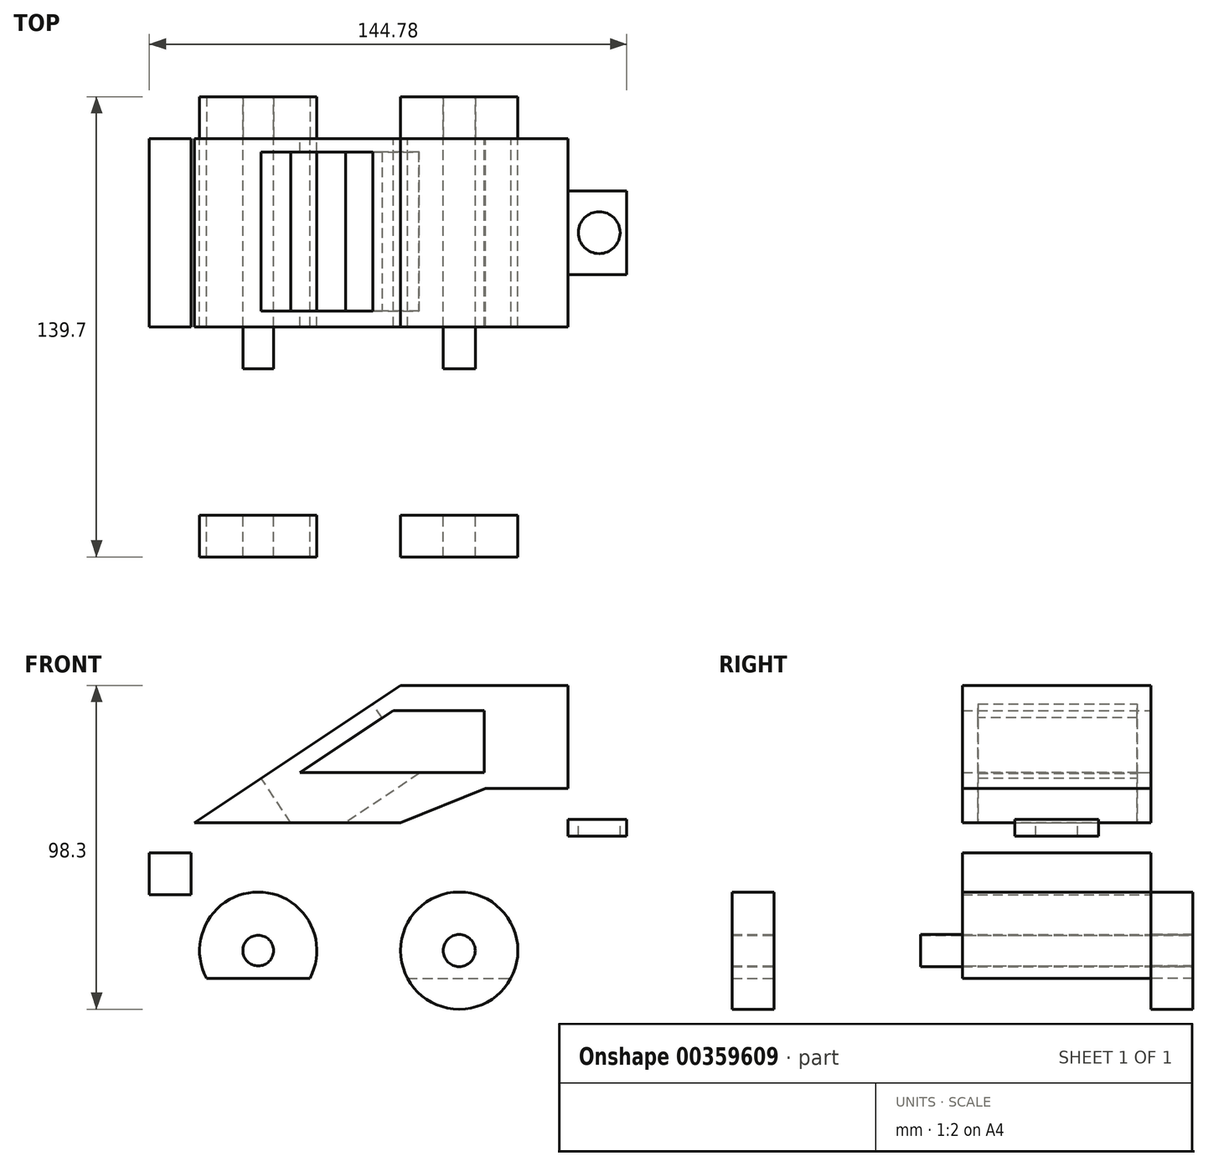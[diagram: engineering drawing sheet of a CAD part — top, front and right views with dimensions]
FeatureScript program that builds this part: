
annotation { "Feature Type Name" : "Feature", "Feature Type Description" : "" }
export const myFeature = defineFeature(function(context is Context, id is Id, definition is map)
    precondition{}
    {
        {
            var Q0;
            Q0=qCreatedBy(makeId("Front.planeOp"),FACE);
            var sketch = newSketch(context, id + "F0", { "sketchPlane" : qUnion([Q0])});
            skLineSegment(sketch, "E0.bottom", {"start": v(13.82, 40.44) * mm, "end": v(64.62, 40.44) * mm});
            skLineSegment(sketch, "E0.top", {"start": v(-62.38, -48.46) * mm, "end": v(64.62, -48.46) * mm});
            skLineSegment(sketch, "E0.left", {"start": v(-62.38, -10.36) * mm, "end": v(-62.38, -48.46) * mm});
            skLineSegment(sketch, "E0.right", {"start": v(64.62, 40.44) * mm, "end": v(64.62, -48.46) * mm});
            skLineSegment(sketch, "E1", {"start": v(-62.38, -10.36) * mm, "end": v(13.82, 40.44) * mm});
            skLineSegment(sketch, "E2.bottom", {"start": v(-62.38, -10.36) * mm, "end": v(-49.68, -10.36) * mm});
            skLineSegment(sketch, "E2.top", {"start": v(-62.38, -23.06) * mm, "end": v(-49.68, -23.06) * mm});
            skLineSegment(sketch, "E2.left", {"start": v(-62.38, -10.36) * mm, "end": v(-62.38, -23.06) * mm});
            skLineSegment(sketch, "E2.right", {"start": v(-49.68, -10.36) * mm, "end": v(-49.68, -23.06) * mm});
            skLineSegment(sketch, "E3", {"start": v(-62.38, -10.36) * mm, "end": v(13.82, -10.36) * mm});
            skLineSegment(sketch, "E4", {"start": v(13.82, -1.24) * mm, "end": v(-48.7, -1.24) * mm});
            skLineSegment(sketch, "E5", {"start": v(39.22, 14) * mm, "end": v(39.22, 32.82) * mm});
            skLineSegment(sketch, "E6", {"start": v(39.22, 14) * mm, "end": v(-16.66, 14) * mm});
            skLineSegment(sketch, "E7", {"start": v(39.22, 32.82) * mm, "end": v(11.58, 32.82) * mm});
            skLineSegment(sketch, "E8", {"start": v(11.58, 32.82) * mm, "end": v(-16.66, 14) * mm});
            skCircle(sketch, "E9", {"center": v(-29.36, -40.08) * mm, "radius": 17.78 * mm});
            skCircle(sketch, "E10", {"center": v(31.6, -40.08) * mm, "radius": 17.78 * mm});
            skCircle(sketch, "E11", {"center": v(-29.36, -40.08) * mm, "radius": 4.65 * mm});
            skCircle(sketch, "E12", {"center": v(31.6, -40.08) * mm, "radius": 4.86 * mm});
            skPoint(sketch, "E13.orphan", {"position": v(-62.38, 40.44) * mm});
            skLineSegment(sketch, "E14", {"start": v(13.82, -1.24) * mm, "end": v(39.6, 9.12) * mm});
            skLineSegment(sketch, "E15", {"start": v(39.6, 9.12) * mm, "end": v(64.62, 9.12) * mm});
            skLineSegment(sketch, "E16", {"start": v(64.62, 0) * mm, "end": v(39.6, 0) * mm});
            skLineSegment(sketch, "E17", {"start": v(39.6, 0) * mm, "end": v(13.82, -10.36) * mm});
            skSolve(sketch);
        }
        {
            var Q0;
            {var subQ1=sQuery(id+"F0.wireOp",EDGE,"E0.bottom");Q0=makeQuery(id+"F0.imprint","IMPRINT",FACE,{"disambiguationData":[TD([[makeQuery(id+"F0.imprint","IMPRINT",EDGE,{"derivedFrom":subQ1}),-1.0]])]});}
            var Q1;
            {var subQ5=sQuery(id+"F0.wireOp",EDGE,"E0.left");Q1=makeQuery(id+"F0.imprint","IMPRINT",FACE,{"disambiguationData":[TD([[makeQuery(id+"F0.imprint","IMPRINT",EDGE,{"derivedFrom":subQ5}),1.0]])]});}
            var Q2;
            Q2=makeQuery(id+"F0.imprint","IMPRINT",FACE,{"disambiguationData":[TD([[makeQuery(id+"F0.imprint","IMPRINT",EDGE,{"derivedFrom":sQuery(id+"F0.wireOp",EDGE,"E11")}),-1.0]])]});
            var Q3;
            Q3=makeQuery(id+"F0.imprint","IMPRINT",FACE,{"disambiguationData":[TD([[makeQuery(id+"F0.imprint","IMPRINT",EDGE,{"derivedFrom":sQuery(id+"F0.wireOp",EDGE,"E12")}),-1.0]])]});
            extrude(context, id + "F1", {"entities" : qUnion([Q0, Q1, Q2, Q3]), "depth" : 57.15 * mm});
        }
        {
            var Q0;
            Q0=makeQuery(id+"F0.imprint","IMPRINT",FACE,{"disambiguationData":[TD([[makeQuery(id+"F0.imprint","IMPRINT",EDGE,{"derivedFrom":sQuery(id+"F0.wireOp",EDGE,"E2.top")}),1.0]])]});
            var Q1;
            {var subQ4=sQuery(id+"F0.wireOp",EDGE,"4A5fvVYB-3RyO-qsuN-9SgG-2Ac1qKv1juyk");Q1=makeQuery(id+"F0.imprint","IMPRINT",FACE,{"disambiguationData":[TD([[makeQuery(id+"F0.imprint","IMPRINT",EDGE,{"derivedFrom":subQ4}),-1.0]])]});}
            extrude(context, id + "F2", {"entities" : qUnion([Q0, Q1]), "depth" : 57.15 * mm});
        }
        {
            var Q0;
            Q0=makeQuery(id+"F0.imprint","IMPRINT",FACE,{"disambiguationData":[TD([[makeQuery(id+"F0.imprint","IMPRINT",EDGE,{"derivedFrom":sQuery(id+"F0.wireOp",EDGE,"E2.top")}),1.0]])]});
            extrude(context, id + "F3", {"entities" : qUnion([Q0]), "depth" : 57.15 * mm});
        }
        {
            var Q0;
            Q0=makeQuery(id+"F0.imprint","IMPRINT",FACE,{"disambiguationData":[TD([[makeQuery(id+"F0.imprint","IMPRINT",EDGE,{"derivedFrom":sQuery(id+"F0.wireOp",EDGE,"E11")}),-1.0]])]});
            var Q1;
            Q1=makeQuery(id+"F0.imprint","IMPRINT",FACE,{"disambiguationData":[TD([[makeQuery(id+"F0.imprint","IMPRINT",EDGE,{"derivedFrom":sQuery(id+"F0.wireOp",EDGE,"E12")}),-1.0]])]});
            var Q2;
            {var subQ0=sQuery(id+"F0.wireOp",EDGE,"E10");var subQ1=sQuery(id+"F0.wireOp",EDGE,"E0.top");var subQ2=makeQuery(id+"F0.imprint","INTERSECT",VERTEX,{"disambiguationData":[OD(0.0)],"derivedFrom":[subQ1,subQ0]});Q2=makeQuery(id+"F0.imprint","IMPRINT",FACE,{"disambiguationData":[TD([[makeQuery(id+"F0.imprint","IMPRINT",EDGE,{"disambiguationData":[TD([[subQ2,-1.0]])],"derivedFrom":subQ1}),-1.0]])]});}
            var Q3;
            {var subQ0=sQuery(id+"F0.wireOp",EDGE,"E9");var subQ1=sQuery(id+"F0.wireOp",EDGE,"E0.top");var subQ2=makeQuery(id+"F0.imprint","INTERSECT",VERTEX,{"disambiguationData":[OD(0.0)],"derivedFrom":[subQ1,subQ0]});Q3=makeQuery(id+"F0.imprint","IMPRINT",FACE,{"disambiguationData":[TD([[makeQuery(id+"F0.imprint","IMPRINT",EDGE,{"disambiguationData":[TD([[subQ2,-1.0]])],"derivedFrom":subQ1}),-1.0]])]});}
            extrude(context, id + "F4", {"entities" : qUnion([Q0, Q1, Q2, Q3]), "oppositeDirection" : true, "depth" : 12.7 * mm});
        }
        {
            var Q0;
            Q0=makeQuery(id+"F4.opExtrude","SWEPT_BODY",BODY,{"disambiguationData":[OSD([sQuery(id+"F0.wireOp",EDGE,"E10"),sQuery(id+"F0.wireOp",EDGE,"E12")])]});
            var Q1;
            Q1=makeQuery(id+"F4.opExtrude","SWEPT_BODY",BODY,{"disambiguationData":[OSD([sQuery(id+"F0.wireOp",EDGE,"E9"),sQuery(id+"F0.wireOp",EDGE,"E11")])]});
            var Q2;
            Q2=makeQuery(id+"F1.opExtrude","CAP_FACE",FACE,{"disambiguationData":[OSD([sQuery(id+"F0.wireOp",EDGE,"E0.top"),sQuery(id+"F0.wireOp",EDGE,"E0.left"),sQuery(id+"F0.wireOp",EDGE,"E0.right"),sQuery(id+"F0.wireOp",EDGE,"E2.top"),sQuery(id+"F0.wireOp",EDGE,"E2.right"),sQuery(id+"F0.wireOp",EDGE,"E3"),sQuery(id+"F0.wireOp",EDGE,"3hkT5JNl-Kwfu-nT25-qYih-FNQphEmEbmh1"),sQuery(id+"F0.wireOp",EDGE,"l82fTogY-9ohq-hUOR-RYja-8vUH1eI0qHhs"),sQuery(id+"F0.wireOp",EDGE,"E11"),sQuery(id+"F0.wireOp",EDGE,"E12")])],"isStart":false});
            mirror(context, id + "F5", {"entities" : qUnion([Q0, Q1]), "mirrorPlane" : qUnion([Q2])});
        }
        {
            var Q0;
            Q0=makeQuery(id+"F1.opExtrude","SWEPT_FACE",FACE,{"disambiguationData":[OSD([sQuery(id+"F0.wireOp",EDGE,"E1")])]});
            var sketch = newSketch(context, id + "F6", { "sketchPlane" : qUnion([Q0])});
            skLineSegment(sketch, "E18.bottom", {"start": v(23.77, -52.44) * mm, "end": v(-16.87, -52.44) * mm});
            skLineSegment(sketch, "E18.top", {"start": v(23.77, -4.18) * mm, "end": v(-16.87, -4.18) * mm});
            skLineSegment(sketch, "E18.left", {"start": v(23.77, -52.44) * mm, "end": v(23.77, -4.18) * mm});
            skLineSegment(sketch, "E18.right", {"start": v(-16.87, -52.44) * mm, "end": v(-16.87, -4.18) * mm});
            skSolve(sketch);
        }
        {
            var Q0;
            Q0 = qSketchRegion(id + "F6", true);
            extrude(context, id + "F7", {"entities" : qUnion([Q0]), "operationType" : NewBodyOperationType.REMOVE, "oppositeDirection" : true, "depth" : 25.4 * mm});
        }
        {
            var Q0;
            {var subQ0=sQuery(id+"F0.wireOp",EDGE,"E0.right");Q0=makeQuery(id+"F1.opExtrude","SWEPT_FACE",FACE,{"disambiguationData":[OSD([subQ0]),TDD([makeQuery(id+"F0.imprint","IMPRINT",EDGE,{"disambiguationData":[TD([[makeQuery(id+"F0.imprint","INTERSECT",VERTEX,{"derivedFrom":[sQuery(id+"F0.wireOp",EDGE,"E0.top"),subQ0]}),1.0]])],"derivedFrom":subQ0})])]});}
            var sketch = newSketch(context, id + "F8", { "sketchPlane" : qUnion([Q0])});
            skLineSegment(sketch, "E19.bottom", {"start": v(-41.27, -0.2) * mm, "end": v(-15.87, -0.2) * mm});
            skLineSegment(sketch, "E19.top", {"start": v(-41.27, -5.28) * mm, "end": v(-15.87, -5.28) * mm});
            skLineSegment(sketch, "E19.left", {"start": v(-41.27, -0.2) * mm, "end": v(-41.27, -5.28) * mm});
            skLineSegment(sketch, "E19.right", {"start": v(-15.87, -0.2) * mm, "end": v(-15.87, -5.28) * mm});
            skSolve(sketch);
        }
        {
            var Q0;
            Q0 = qSketchRegion(id + "F8", true);
            extrude(context, id + "F9", {"entities" : qUnion([Q0]), "operationType" : NewBodyOperationType.ADD, "depth" : 17.78 * mm});
        }
        {
            var Q0;
            Q0=makeQuery(id+"F9.opExtrude","SWEPT_FACE",FACE,{"disambiguationData":[OSD([sQuery(id+"F8.wireOp",EDGE,"E19.bottom")])]});
            var sketch = newSketch(context, id + "F10", { "sketchPlane" : qUnion([Q0])});
            skCircle(sketch, "E20", {"center": v(74.05, -28.59) * mm, "radius": 6.35 * mm});
            skSolve(sketch);
        }
        {
            var Q0;
            Q0 = qSketchRegion(id + "F10", true);
            extrude(context, id + "F11", {"entities" : qUnion([Q0]), "operationType" : NewBodyOperationType.REMOVE, "oppositeDirection" : true, "depth" : 25.4 * mm});
        }
        {
            var Q0;
            Q0=makeQuery(id+"F4.opExtrude","CAP_FACE",FACE,{"disambiguationData":[OSD([sQuery(id+"F0.wireOp",EDGE,"E9"),sQuery(id+"F0.wireOp",EDGE,"E11")])],"isStart":false});
            var sketch = newSketch(context, id + "F12", { "sketchPlane" : qUnion([Q0])});
            skCircle(sketch, "E21", {"center": v(29.36, -40.08) * mm, "radius": 4.65 * mm});
            skSolve(sketch);
        }
        {
            var Q0;
            Q0 = qSketchRegion(id + "F12", true);
            extrude(context, id + "F13", {"entities" : qUnion([Q0]), "oppositeDirection" : true, "depth" : 82.55 * mm});
        }
        {
            var Q0;
            Q0=makeQuery(id+"F0.imprint","IMPRINT",FACE,{"disambiguationData":[TD([[makeQuery(id+"F0.imprint","IMPRINT",EDGE,{"derivedFrom":sQuery(id+"F0.wireOp",EDGE,"E12")}),1.0]])]});
            var Q1;
            Q1=sQuery(id+"F0.wireOp",EDGE,"E12");
            extrude(context, id + "F14", {"entities" : qUnion([Q0]), "surfaceEntities" : qUnion([Q1]), "depth" : 69.85 * mm, "hasSecondDirection" : true, "secondDirectionOppositeDirection" : true, "secondDirectionDepth" : 12.7 * mm});
        }
    });
